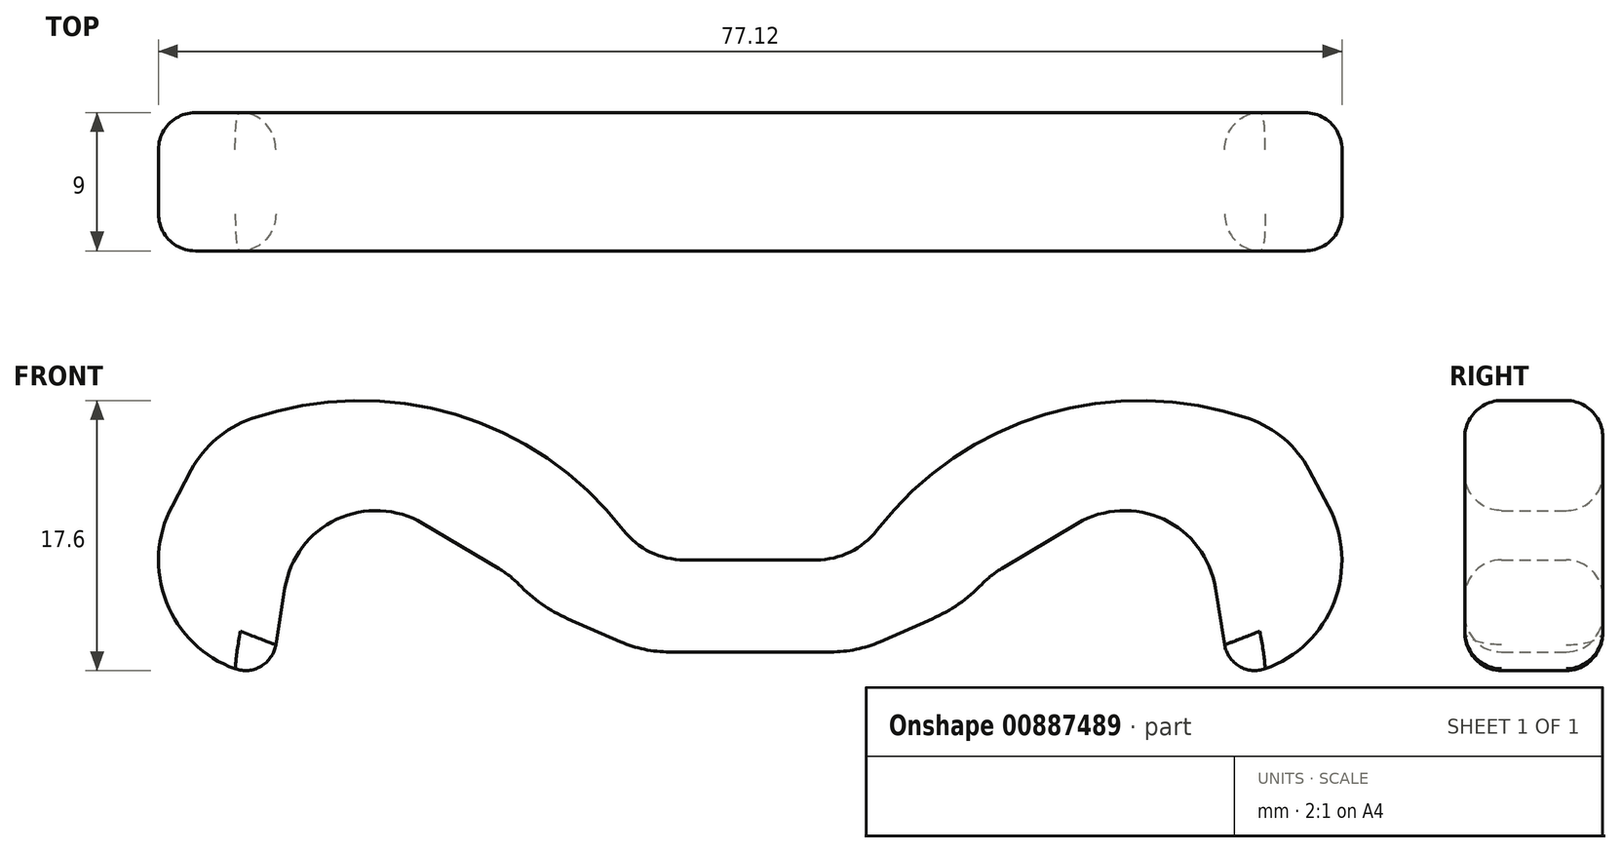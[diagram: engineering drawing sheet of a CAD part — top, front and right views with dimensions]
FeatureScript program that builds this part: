
annotation { "Feature Type Name" : "Feature", "Feature Type Description" : "" }
export const myFeature = defineFeature(function(context is Context, id is Id, definition is map)
    precondition{}
    {
        {
            var Q0;
            Q0=qCreatedBy(makeId("Front.planeOp"),FACE);
            var sketch = newSketch(context, id + "F0", { "sketchPlane" : qUnion([Q0])});
            skLineSegment(sketch, "E0.bottom", {"start": v(36, -27.02) * mm, "end": v(-36, -27.02) * mm, "construction": true});
            skLineSegment(sketch, "E0.top", {"start": v(36, 27.02) * mm, "end": v(-36, 27.02) * mm, "construction": true});
            skLineSegment(sketch, "E0.left", {"start": v(36, -27.02) * mm, "end": v(36, 27.02) * mm, "construction": true});
            skLineSegment(sketch, "E0.right", {"start": v(-36, -27.02) * mm, "end": v(-36, 27.02) * mm, "construction": true});
            skLineSegment(sketch, "E1", {"start": v(-28.43, 25.32) * mm, "end": v(-7.26, 16.04) * mm});
            skLineSegment(sketch, "E2", {"start": v(-35.47, 20.95) * mm, "end": v(-34.2, 23.31) * mm});
            skLineSegment(sketch, "E3", {"start": v(-34.86, 15.35) * mm, "end": v(-28.8, 8.24) * mm});
            skLineSegment(sketch, "E4", {"start": v(-27.92, 6.4) * mm, "end": v(-26.68, 0) * mm});
            skPoint(sketch, "E5.visualSharp", {"position": v(-28.12, 7.43) * mm});
            skArc(sketch, "E5.filletArc", {"start": v(-27.92, 6.4) * mm, "mid": v(-28.24, 7.37) * mm, "end": v(-28.8, 8.24) * mm});
            skPoint(sketch, "E6.visualSharp", {"position": v(-32.25, 27) * mm});
            skArc(sketch, "E6.filletArc", {"start": v(-28.43, 25.32) * mm, "mid": v(-31.71, 25.45) * mm, "end": v(-34.2, 23.31) * mm});
            skPoint(sketch, "E7.visualSharp", {"position": v(-37.07, 17.94) * mm});
            skArc(sketch, "E7.filletArc", {"start": v(-35.47, 20.95) * mm, "mid": v(-36.03, 18.06) * mm, "end": v(-34.86, 15.35) * mm});
            skPoint(sketch, "E8.visualSharp", {"position": v(-6.3, 15.62) * mm});
            skArc(sketch, "E8.filletArc", {"start": v(-7.26, 16.04) * mm, "mid": v(-6.28, 15.73) * mm, "end": v(-5.26, 15.62) * mm});
            skCircle(sketch, "E9", {"center": v(-24.4, 15.84) * mm, "radius": 2 * mm, "construction": true});
            skCircle(sketch, "E10", {"center": v(-24.4, 15.84) * mm, "radius": 6 * mm});
            skArc(sketch, "E11.0", {"start": v(-37.67, 22.12) * mm, "mid": v(-38.05, 15.88) * mm, "end": v(-33.56, 11.52) * mm});
            skLineSegment(sketch, "E11.1", {"start": v(-37.67, 22.12) * mm, "end": v(-36.41, 24.49) * mm});
            skArc(sketch, "E11.2", {"start": v(-27.43, 27.6) * mm, "mid": v(-32.53, 27.8) * mm, "end": v(-36.41, 24.49) * mm});
            skLineSegment(sketch, "E11.3", {"start": v(-27.43, 27.6) * mm, "end": v(-6.92, 18.62) * mm});
            skLineSegment(sketch, "E12", {"start": v(-30.92, 13.1) * mm, "end": v(-30.32, 16.8) * mm});
            skPoint(sketch, "E13.visualSharp", {"position": v(-31.24, 11.1) * mm});
            skArc(sketch, "E13.filletArc", {"start": v(-33.56, 11.52) * mm, "mid": v(-31.87, 11.69) * mm, "end": v(-30.92, 13.1) * mm});
            skLineSegment(sketch, "E14", {"start": v(-5.26, 15.62) * mm, "end": v(0, 15.62) * mm});
            skLineSegment(sketch, "E15", {"start": v(-4.3, 18.62) * mm, "end": v(0, 18.62) * mm});
            skPoint(sketch, "E16.visualSharp", {"position": v(-6.92, 18.62) * mm});
            skArc(sketch, "E17", {"start": v(-8.26, 20.57) * mm, "mid": v(-19.23, 28.1) * mm, "end": v(-32.53, 27.8) * mm});
            skLineSegment(sketch, "E18.MirrorCS", {"start": v(37.67, 22.12) * mm, "end": v(36.41, 24.49) * mm});
            skLineSegment(sketch, "E19.MirrorCS", {"start": v(35.47, 20.95) * mm, "end": v(34.2, 23.31) * mm});
            skArc(sketch, "E20.MirrorCS", {"start": v(27.92, 6.4) * mm, "mid": v(28.24, 7.37) * mm, "end": v(28.8, 8.24) * mm});
            skArc(sketch, "E21.MirrorCS", {"start": v(33.56, 11.52) * mm, "mid": v(31.87, 11.69) * mm, "end": v(30.92, 13.1) * mm});
            skArc(sketch, "E22.MirrorCS", {"start": v(7.26, 16.04) * mm, "mid": v(6.28, 15.73) * mm, "end": v(5.26, 15.62) * mm});
            skPoint(sketch, "E23.MirrorP", {"position": v(32.25, 27) * mm});
            skLineSegment(sketch, "E24.MirrorCS", {"start": v(5.26, 15.62) * mm, "end": v(0, 15.62) * mm});
            skPoint(sketch, "E25.MirrorP", {"position": v(6.3, 15.62) * mm});
            skArc(sketch, "E26.MirrorCS", {"start": v(27.43, 27.6) * mm, "mid": v(32.53, 27.8) * mm, "end": v(36.41, 24.49) * mm});
            skLineSegment(sketch, "E27.MirrorCS", {"start": v(30.92, 13.1) * mm, "end": v(30.32, 16.8) * mm});
            skLineSegment(sketch, "E28.MirrorCS", {"start": v(27.92, 6.4) * mm, "end": v(26.68, 0) * mm});
            skLineSegment(sketch, "E29.MirrorCS", {"start": v(34.86, 15.35) * mm, "end": v(28.8, 8.24) * mm});
            skLineSegment(sketch, "E30.MirrorCS", {"start": v(28.43, 25.32) * mm, "end": v(7.26, 16.04) * mm});
            skCircle(sketch, "E31.MirrorC", {"center": v(24.4, 15.84) * mm, "radius": 6 * mm});
            skPoint(sketch, "E32.MirrorP", {"position": v(31.24, 11.1) * mm});
            skPoint(sketch, "E33.MirrorP", {"position": v(28.12, 7.43) * mm});
            skArc(sketch, "E34.MirrorCS", {"start": v(37.67, 22.12) * mm, "mid": v(38.05, 15.88) * mm, "end": v(33.56, 11.52) * mm});
            skArc(sketch, "E35.MirrorCS", {"start": v(28.43, 25.32) * mm, "mid": v(31.71, 25.45) * mm, "end": v(34.2, 23.31) * mm});
            skArc(sketch, "E36.MirrorCS", {"start": v(35.47, 20.95) * mm, "mid": v(36.03, 18.06) * mm, "end": v(34.86, 15.35) * mm});
            skCircle(sketch, "E37.MirrorC", {"center": v(24.4, 15.84) * mm, "radius": 2 * mm, "construction": true});
            skPoint(sketch, "E38.MirrorP", {"position": v(37.07, 17.94) * mm});
            skCircle(sketch, "E39", {"center": v(-19.42, 12.89) * mm, "radius": 2 * mm, "construction": true});
            skCircle(sketch, "E40", {"center": v(-19.42, 12.89) * mm, "radius": 6 * mm});
            skLineSegment(sketch, "E41", {"start": v(-21.33, 21) * mm, "end": v(-16.36, 18.05) * mm});
            skLineSegment(sketch, "E42.0", {"start": v(-5.26, 12.62) * mm, "end": v(0, 12.62) * mm});
            skArc(sketch, "E42.1", {"start": v(-8.47, 13.3) * mm, "mid": v(-6.9, 12.8) * mm, "end": v(-5.26, 12.62) * mm});
            skLineSegment(sketch, "E42.2", {"start": v(-14.18, 15.8) * mm, "end": v(-8.47, 13.3) * mm});
            skArc(sketch, "E43", {"start": v(-15.09, 17.03) * mm, "mid": v(-13.6, 15.75) * mm, "end": v(-11.88, 14.79) * mm});
            skLineSegment(sketch, "E44.MirrorCS", {"start": v(5.26, 12.62) * mm, "end": v(0, 12.62) * mm});
            skLineSegment(sketch, "E45.MirrorCS", {"start": v(14.18, 15.8) * mm, "end": v(8.47, 13.3) * mm});
            skLineSegment(sketch, "E46.MirrorCS", {"start": v(21.33, 21) * mm, "end": v(16.36, 18.05) * mm});
            skCircle(sketch, "E47.MirrorC", {"center": v(19.42, 12.89) * mm, "radius": 6 * mm});
            skArc(sketch, "E48.MirrorCS", {"start": v(15.09, 17.03) * mm, "mid": v(13.6, 15.75) * mm, "end": v(11.88, 14.79) * mm});
            skArc(sketch, "E49.MirrorCS", {"start": v(8.47, 13.3) * mm, "mid": v(6.9, 12.8) * mm, "end": v(5.26, 12.62) * mm});
            skArc(sketch, "E50.filletArc", {"start": v(-8.26, 20.57) * mm, "mid": v(-6.5, 19.13) * mm, "end": v(-4.3, 18.62) * mm});
            skLineSegment(sketch, "E51.MirrorCS", {"start": v(27.43, 27.6) * mm, "end": v(6.92, 18.62) * mm});
            skLineSegment(sketch, "E52.MirrorCS", {"start": v(4.3, 18.62) * mm, "end": v(0, 18.62) * mm});
            skArc(sketch, "E53.MirrorCS", {"start": v(8.26, 20.57) * mm, "mid": v(6.5, 19.13) * mm, "end": v(4.3, 18.62) * mm});
            skArc(sketch, "E54.MirrorCS", {"start": v(8.26, 20.57) * mm, "mid": v(19.23, 28.1) * mm, "end": v(32.53, 27.8) * mm});
            skSolve(sketch);
        }
        {
            var Q0;
            {var subQ0=sQuery(id+"F0.wireOp",EDGE,"E8.filletArc");var subQ1=sQuery(id+"F0.wireOp",EDGE,"E1");var subQ2=makeQuery(id+"F0.imprint","INTERSECT",VERTEX,{"derivedFrom":[subQ1,subQ0]});Q0=makeQuery(id+"F0.imprint","IMPRINT",FACE,{"disambiguationData":[TD([[makeQuery(id+"F0.imprint","IMPRINT",EDGE,{"disambiguationData":[TD([[subQ2,1.0]])],"derivedFrom":subQ1}),1.0]])]});}
            var Q1;
            Q1=makeQuery(id+"F0.imprint","IMPRINT",FACE,{"disambiguationData":[TD([[makeQuery(id+"F0.imprint","IMPRINT",EDGE,{"derivedFrom":sQuery(id+"F0.wireOp",EDGE,"E2")}),1.0]])]});
            var Q2;
            {var subQ0=sQuery(id+"F0.wireOp",EDGE,"01ceb5dc-e233-417b-8349-8d012c69cf2a18.MirrorCS");var subQ1=sQuery(id+"F0.wireOp",EDGE,"01ceb5dc-e233-417b-8349-8d012c69cf2a4.MirrorCS");var subQ2=makeQuery(id+"F0.imprint","INTERSECT",VERTEX,{"derivedFrom":[subQ1,subQ0]});Q2=makeQuery(id+"F0.imprint","IMPRINT",FACE,{"disambiguationData":[TD([[makeQuery(id+"F0.imprint","IMPRINT",EDGE,{"disambiguationData":[TD([[subQ2,-1.0]])],"derivedFrom":subQ1}),-1.0]])]});}
            var Q3;
            {var subQ0=sQuery(id+"F0.wireOp",EDGE,"3262a955-999c-468b-b28b-10104bbbcd4b17.MirrorCS");var subQ1=sQuery(id+"F0.wireOp",EDGE,"3262a955-999c-468b-b28b-10104bbbcd4b3.MirrorCS");var subQ2=makeQuery(id+"F0.imprint","INTERSECT",VERTEX,{"derivedFrom":[subQ1,subQ0]});Q3=makeQuery(id+"F0.imprint","IMPRINT",FACE,{"disambiguationData":[TD([[makeQuery(id+"F0.imprint","IMPRINT",EDGE,{"disambiguationData":[TD([[subQ2,-1.0]])],"derivedFrom":subQ1}),-1.0]])]});}
            var Q4;
            {var subQ0=sQuery(id+"F0.wireOp",EDGE,"E11.3");Q4=makeQuery(id+"F0.imprint","IMPRINT",FACE,{"disambiguationData":[TD([[makeQuery(id+"F0.imprint","IMPRINT",EDGE,{"derivedFrom":subQ0}),1.0]])]});}
            var Q5;
            {var subQ0=sQuery(id+"F0.wireOp",EDGE,"E30.MirrorCS");var subQ1=sQuery(id+"F0.wireOp",EDGE,"E22.MirrorCS");var subQ2=makeQuery(id+"F0.imprint","INTERSECT",VERTEX,{"derivedFrom":[subQ1,subQ0]});Q5=makeQuery(id+"F0.imprint","IMPRINT",FACE,{"disambiguationData":[TD([[makeQuery(id+"F0.imprint","IMPRINT",EDGE,{"disambiguationData":[TD([[subQ2,-1.0]])],"derivedFrom":subQ1}),-1.0]])]});}
            extrude(context, id + "F1", {"entities" : qUnion([Q0, Q1, Q2, Q3, Q4, Q5]), "depth" : 9 * mm, "offsetDistance" : 25 * mm, "symmetric" : true});
        }
        {
            var Q0;
            Q0=makeQuery(id+"F0.imprint","IMPRINT",FACE,{"disambiguationData":[TD([[makeQuery(id+"F0.imprint","IMPRINT",EDGE,{"derivedFrom":sQuery(id+"F0.wireOp",EDGE,"E2")}),-1.0]])]});
            var Q1;
            {var subQ3=sQuery(id+"F0.wireOp",EDGE,"E1");var subQ5=sQuery(id+"F0.wireOp",EDGE,"E8.filletArc");var subQ6=makeQuery(id+"F0.imprint","INTERSECT",VERTEX,{"derivedFrom":[subQ3,subQ5]});Q1=makeQuery(id+"F0.imprint","IMPRINT",FACE,{"disambiguationData":[TD([[makeQuery(id+"F0.imprint","IMPRINT",EDGE,{"disambiguationData":[TD([[subQ6,1.0]])],"derivedFrom":subQ3}),-1.0]])]});}
            var Q2;
            {var subQ4=sQuery(id+"F0.wireOp",EDGE,"E14");Q2=makeQuery(id+"F0.imprint","IMPRINT",FACE,{"disambiguationData":[TD([[makeQuery(id+"F0.imprint","IMPRINT",EDGE,{"derivedFrom":subQ4}),-1.0]])]});}
            var Q3;
            {var subQ3=sQuery(id+"F0.wireOp",EDGE,"01ceb5dc-e233-417b-8349-8d012c69cf2a18.MirrorCS");var subQ5=sQuery(id+"F0.wireOp",EDGE,"01ceb5dc-e233-417b-8349-8d012c69cf2a4.MirrorCS");var subQ6=makeQuery(id+"F0.imprint","INTERSECT",VERTEX,{"derivedFrom":[subQ5,subQ3]});Q3=makeQuery(id+"F0.imprint","IMPRINT",FACE,{"disambiguationData":[TD([[makeQuery(id+"F0.imprint","IMPRINT",EDGE,{"disambiguationData":[TD([[subQ6,-1.0]])],"derivedFrom":subQ5}),1.0]])]});}
            var Q4;
            Q4=makeQuery(id+"F0.imprint","IMPRINT",FACE,{"disambiguationData":[TD([[makeQuery(id+"F0.imprint","IMPRINT",EDGE,{"derivedFrom":sQuery(id+"F0.wireOp",EDGE,"01ceb5dc-e233-417b-8349-8d012c69cf2a1.MirrorCS")}),1.0]])]});
            var Q5;
            {var subQ3=sQuery(id+"F0.wireOp",EDGE,"3262a955-999c-468b-b28b-10104bbbcd4b17.MirrorCS");var subQ5=sQuery(id+"F0.wireOp",EDGE,"3262a955-999c-468b-b28b-10104bbbcd4b3.MirrorCS");var subQ6=makeQuery(id+"F0.imprint","INTERSECT",VERTEX,{"derivedFrom":[subQ5,subQ3]});Q5=makeQuery(id+"F0.imprint","IMPRINT",FACE,{"disambiguationData":[TD([[makeQuery(id+"F0.imprint","IMPRINT",EDGE,{"disambiguationData":[TD([[subQ6,-1.0]])],"derivedFrom":subQ5}),1.0]])]});}
            var Q6;
            Q6=makeQuery(id+"F0.imprint","IMPRINT",FACE,{"disambiguationData":[TD([[makeQuery(id+"F0.imprint","IMPRINT",EDGE,{"derivedFrom":sQuery(id+"F0.wireOp",EDGE,"3262a955-999c-468b-b28b-10104bbbcd4b1.MirrorCS")}),1.0]])]});
            var Q7;
            {var subQ3=sQuery(id+"F0.wireOp",EDGE,"E30.MirrorCS");var subQ4=sQuery(id+"F0.wireOp",EDGE,"E22.MirrorCS");var subQ5=makeQuery(id+"F0.imprint","INTERSECT",VERTEX,{"derivedFrom":[subQ4,subQ3]});Q7=makeQuery(id+"F0.imprint","IMPRINT",FACE,{"disambiguationData":[TD([[makeQuery(id+"F0.imprint","IMPRINT",EDGE,{"disambiguationData":[TD([[subQ5,-1.0]])],"derivedFrom":subQ4}),1.0]])]});}
            var Q8;
            Q8=makeQuery(id+"F0.imprint","IMPRINT",FACE,{"disambiguationData":[TD([[makeQuery(id+"F0.imprint","IMPRINT",EDGE,{"derivedFrom":sQuery(id+"F0.wireOp",EDGE,"E19.MirrorCS")}),1.0]])]});
            extrude(context, id + "F2", {"entities" : qUnion([Q0, Q1, Q2, Q3, Q4, Q5, Q6, Q7, Q8]), "depth" : 4.5 * mm, "offsetDistance" : 25 * mm, "hasSecondDirection" : true, "secondDirectionOppositeDirection" : false, "secondDirectionDepth" : 2.1 * mm});
        }
        {
            var Q0;
            Q0=makeQuery(id+"F2.opExtrude","SWEPT_BODY",BODY,{"disambiguationData":[OSD([sQuery(id+"F0.wireOp",EDGE,"E1"),sQuery(id+"F0.wireOp",EDGE,"E2"),sQuery(id+"F0.wireOp",EDGE,"E3"),sQuery(id+"F0.wireOp",EDGE,"E6.filletArc"),sQuery(id+"F0.wireOp",EDGE,"E7.filletArc"),sQuery(id+"F0.wireOp",EDGE,"E8.filletArc"),sQuery(id+"F0.wireOp",EDGE,"E10"),sQuery(id+"F0.wireOp",EDGE,"E12"),sQuery(id+"F0.wireOp",EDGE,"E13.filletArc"),sQuery(id+"F0.wireOp",EDGE,"cpl2RN6t-5Irv-f1aV-cCLq-CrQK6vZGKYLU"),sQuery(id+"F0.wireOp",EDGE,"jMhcwcy6-BU4I-j8nz-enuD-g4OT3ZrHSKQ1"),sQuery(id+"F0.wireOp",EDGE,"E14"),sQuery(id+"F0.wireOp",EDGE,"01ceb5dc-e233-417b-8349-8d012c69cf2a1.MirrorCS"),sQuery(id+"F0.wireOp",EDGE,"01ceb5dc-e233-417b-8349-8d012c69cf2a4.MirrorCS"),sQuery(id+"F0.wireOp",EDGE,"01ceb5dc-e233-417b-8349-8d012c69cf2a5.MirrorCS"),sQuery(id+"F0.wireOp",EDGE,"01ceb5dc-e233-417b-8349-8d012c69cf2a6.MirrorCS"),sQuery(id+"F0.wireOp",EDGE,"01ceb5dc-e233-417b-8349-8d012c69cf2a9.MirrorCS"),sQuery(id+"F0.wireOp",EDGE,"01ceb5dc-e233-417b-8349-8d012c69cf2a10.MirrorCS"),sQuery(id+"F0.wireOp",EDGE,"01ceb5dc-e233-417b-8349-8d012c69cf2a12.MirrorCS"),sQuery(id+"F0.wireOp",EDGE,"01ceb5dc-e233-417b-8349-8d012c69cf2a13.MirrorCS"),sQuery(id+"F0.wireOp",EDGE,"01ceb5dc-e233-417b-8349-8d012c69cf2a18.MirrorCS"),sQuery(id+"F0.wireOp",EDGE,"01ceb5dc-e233-417b-8349-8d012c69cf2a21.MirrorC"),sQuery(id+"F0.wireOp",EDGE,"01ceb5dc-e233-417b-8349-8d012c69cf2a24.MirrorC"),sQuery(id+"F0.wireOp",EDGE,"01ceb5dc-e233-417b-8349-8d012c69cf2a27.MirrorCS"),sQuery(id+"F0.wireOp",EDGE,"QKPtNEIy-VxiL-y0EJ-i9cW-Jv92YwvaRkE8"),sQuery(id+"F0.wireOp",EDGE,"36023bd6-33f4-4002-a5ba-531925a0bd500.MirrorCS")])]});
            var Q1;
            Q1=qCreatedBy(makeId("Front.planeOp"),FACE);
            mirror(context, id + "F3", {"operationType" : NewBodyOperationType.ADD, "entities" : qUnion([Q0]), "mirrorPlane" : qUnion([Q1])});
        }
        {
            var Q0;
            Q0=makeQuery(id+"F1.opExtrude","CAP_EDGE",EDGE,{"disambiguationData":[OSD([sQuery(id+"F0.wireOp",EDGE,"E15"),sQuery(id+"F0.wireOp",EDGE,"01ceb5dc-e233-417b-8349-8d012c69cf2a7.MirrorCS")])],"isStart":false});
            var Q1;
            Q1=makeQuery(id+"F1.opExtrude","CAP_EDGE",EDGE,{"disambiguationData":[OSD([sQuery(id+"F0.wireOp",EDGE,"E15"),sQuery(id+"F0.wireOp",EDGE,"01ceb5dc-e233-417b-8349-8d012c69cf2a7.MirrorCS")])],"isStart":true});
            fillet(context, id + "F4", {"entities" : qUnion([Q0, Q1]), "radius" : 2.4 * mm, "tangentPropagation" : true, "allowEdgeOverflow" : false});
        }
    });
